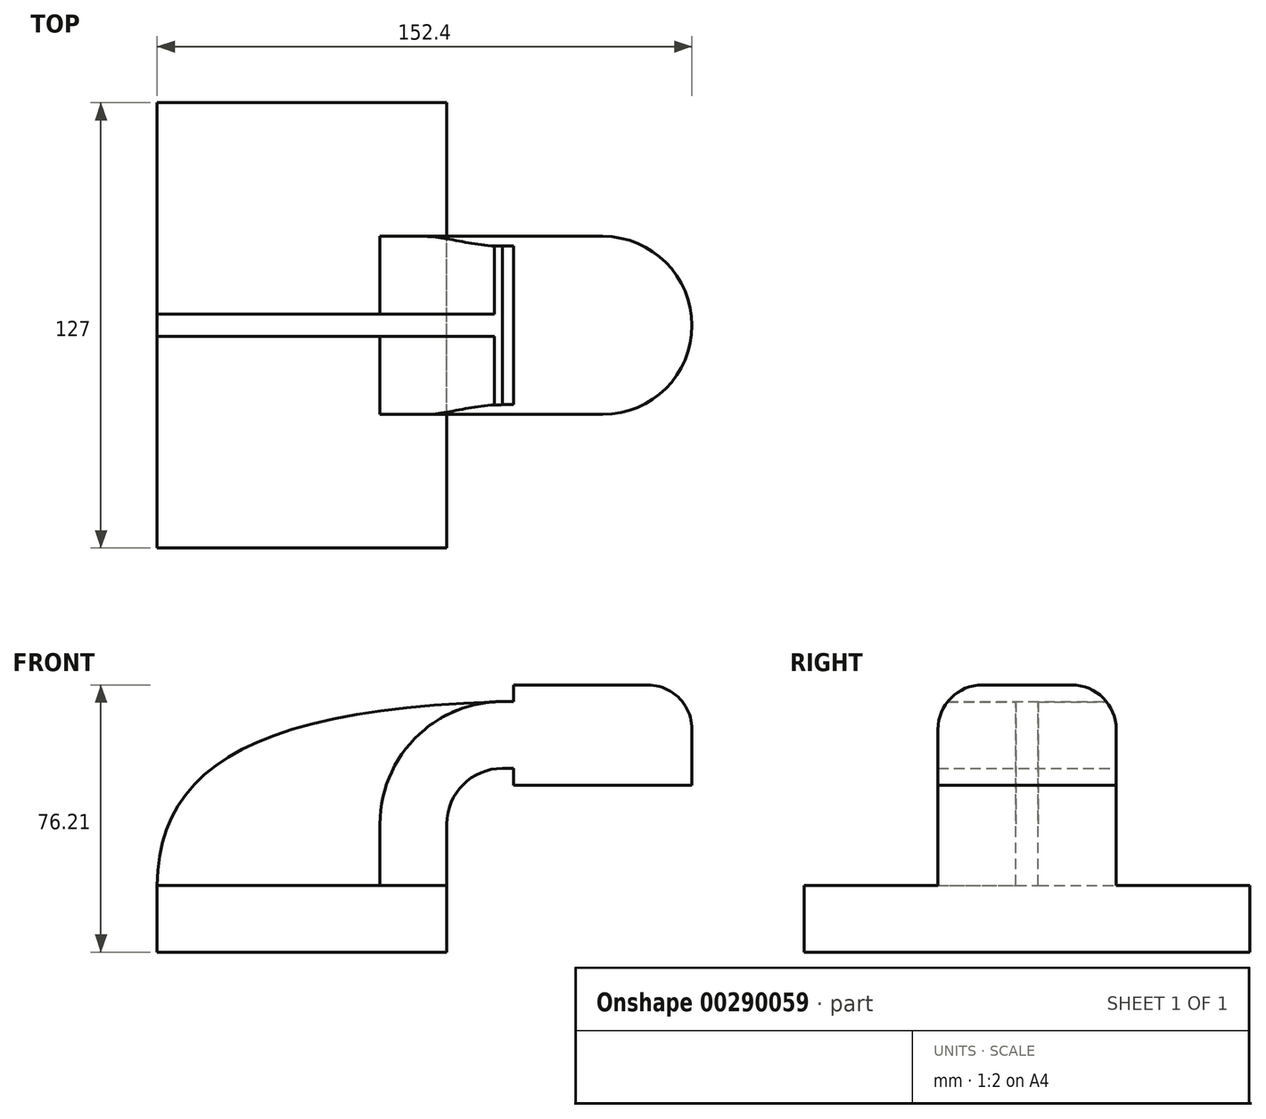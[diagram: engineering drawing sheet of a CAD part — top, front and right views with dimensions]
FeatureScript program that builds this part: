
annotation { "Feature Type Name" : "Feature", "Feature Type Description" : "" }
export const myFeature = defineFeature(function(context is Context, id is Id, definition is map)
    precondition{}
    {
        {
            var Q0;
            Q0=qCreatedBy(makeId("Front.planeOp"),FACE);
            var sketch = newSketch(context, id + "F0", { "sketchPlane" : qUnion([Q0])});
            skLineSegment(sketch, "E0.bottom", {"start": v(-41.28, -9.52) * mm, "end": v(41.28, -9.52) * mm});
            skLineSegment(sketch, "E0.top", {"start": v(-41.28, 9.53) * mm, "end": v(41.28, 9.53) * mm});
            skLineSegment(sketch, "E0.left", {"start": v(-41.28, -9.52) * mm, "end": v(-41.28, 9.53) * mm});
            skLineSegment(sketch, "E0.right", {"start": v(41.28, -9.52) * mm, "end": v(41.28, 9.53) * mm});
            skPoint(sketch, "E0.middle", {"position": v(0, 0) * mm});
            skLineSegment(sketch, "E1.bottom", {"start": v(111.12, 38.1) * mm, "end": v(60.33, 38.1) * mm});
            skLineSegment(sketch, "E1.top", {"start": v(111.13, 66.68) * mm, "end": v(60.33, 66.68) * mm});
            skLineSegment(sketch, "E1.left", {"start": v(111.12, 38.1) * mm, "end": v(111.12, 66.68) * mm});
            skLineSegment(sketch, "E1.right", {"start": v(60.33, 38.1) * mm, "end": v(60.33, 66.68) * mm});
            skPoint(sketch, "E1.middle", {"position": v(85.73, 52.39) * mm});
            skLineSegment(sketch, "E2", {"start": v(41.28, 9.53) * mm, "end": v(41.28, 27) * mm});
            skArc(sketch, "E3", {"start": v(41.28, 27) * mm, "mid": v(45.92, 38.23) * mm, "end": v(57.15, 42.88) * mm});
            skLineSegment(sketch, "E4", {"start": v(57.15, 42.88) * mm, "end": v(85.72, 42.88) * mm});
            skLineSegment(sketch, "E5.0", {"start": v(57.15, 61.93) * mm, "end": v(85.72, 61.93) * mm});
            skArc(sketch, "E5.1", {"start": v(22.23, 27) * mm, "mid": v(32.45, 51.7) * mm, "end": v(57.15, 61.93) * mm});
            skLineSegment(sketch, "E5.2", {"start": v(22.23, 9.53) * mm, "end": v(22.23, 27) * mm});
            skLineSegment(sketch, "E6", {"start": v(85.73, 38.1) * mm, "end": v(85.73, 66.68) * mm});
            skFitSpline(sketch, "E7", {"points": [v(-41.28, 9.53) * mm, v(57.15, 61.93) * mm], "startDerivative": vector(1.5, 100.69) * mm, "endDerivative": vector(213.45, 6.46) * mm});
            skSolve(sketch);
        }
        {
            var Q0;
            Q0=makeQuery(id+"F0.imprint","IMPRINT",FACE,{"disambiguationData":[TD([[makeQuery(id+"F0.imprint","IMPRINT",EDGE,{"derivedFrom":sQuery(id+"F0.wireOp",EDGE,"E0.bottom")}),1.0]])]});
            extrude(context, id + "F1", {"entities" : qUnion([Q0]), "endBound" : BoundingType.SYMMETRIC, "depth" : 127 * mm});
        }
        {
            var Q0;
            {var subQ1=sQuery(id+"F0.wireOp",EDGE,"E2");Q0=makeQuery(id+"F0.imprint","IMPRINT",FACE,{"disambiguationData":[TD([[makeQuery(id+"F0.imprint","IMPRINT",EDGE,{"derivedFrom":subQ1}),1.0]])]});}
            var Q1;
            {var subQ0=sQuery(id+"F0.wireOp",EDGE,"E4");var subQ1=sQuery(id+"F0.wireOp",EDGE,"E1.right");var subQ2=makeQuery(id+"F0.imprint","INTERSECT",VERTEX,{"derivedFrom":[subQ1,subQ0]});Q1=makeQuery(id+"F0.imprint","IMPRINT",FACE,{"disambiguationData":[TD([[makeQuery(id+"F0.imprint","IMPRINT",EDGE,{"disambiguationData":[TD([[subQ2,-1.0]])],"derivedFrom":subQ1}),-1.0]])]});}
            var Q2;
            {var subQ0=sQuery(id+"F0.wireOp",EDGE,"E1.right");var subQ1=sQuery(id+"F0.wireOp",EDGE,"E1.top");var subQ2=makeQuery(id+"F0.imprint","INTERSECT",VERTEX,{"derivedFrom":[subQ1,subQ0]});Q2=makeQuery(id+"F0.imprint","IMPRINT",FACE,{"disambiguationData":[TD([[makeQuery(id+"F0.imprint","IMPRINT",EDGE,{"disambiguationData":[TD([[subQ2,1.0]])],"derivedFrom":subQ1}),1.0]])]});}
            var Q3;
            {var subQ0=sQuery(id+"F0.wireOp",EDGE,"E1.right");var subQ1=sQuery(id+"F0.wireOp",EDGE,"E1.bottom");var subQ2=makeQuery(id+"F0.imprint","INTERSECT",VERTEX,{"derivedFrom":[subQ1,subQ0]});Q3=makeQuery(id+"F0.imprint","IMPRINT",FACE,{"disambiguationData":[TD([[makeQuery(id+"F0.imprint","IMPRINT",EDGE,{"disambiguationData":[TD([[subQ2,1.0]])],"derivedFrom":subQ1}),-1.0]])]});}
            extrude(context, id + "F2", {"entities" : qUnion([Q0, Q1, Q2, Q3]), "operationType" : NewBodyOperationType.ADD, "endBound" : BoundingType.SYMMETRIC, "depth" : 50.8 * mm});
        }
        {
            var Q0;
            {var subQ0=sQuery(id+"F0.wireOp",EDGE,"E1.left");Q0=makeQuery(id+"F0.imprint","IMPRINT",FACE,{"disambiguationData":[TD([[makeQuery(id+"F0.imprint","IMPRINT",EDGE,{"derivedFrom":subQ0}),1.0]])]});}
            var Q1;
            Q1=sQuery(id+"F0.wireOp",EDGE,"E6");
            revolve(context, id + "F3", {"operationType" : NewBodyOperationType.ADD, "entities" : qUnion([Q0]), "axis" : qUnion([Q1]), "revolveType" : RevolveType.FULL});
        }
        {
            var Q0;
            {var subQ3=sQuery(id+"F0.wireOp",EDGE,"E5.2");Q0=makeQuery(id+"F0.imprint","IMPRINT",FACE,{"disambiguationData":[TD([[makeQuery(id+"F0.imprint","IMPRINT",EDGE,{"derivedFrom":subQ3}),1.0]])]});}
            extrude(context, id + "F4", {"entities" : qUnion([Q0]), "operationType" : NewBodyOperationType.ADD, "endBound" : BoundingType.SYMMETRIC, "depth" : 6.35 * mm});
        }
        {
            var Q0;
            Q0=makeQuery(id+"F3.opRevolve","SWEPT_EDGE",EDGE,{"disambiguationData":[OSD([sQuery(id+"F0.wireOp",EDGE,"E1.top"),sQuery(id+"F0.wireOp",EDGE,"E1.left")])]});
            fillet(context, id + "F5", {"entities" : qUnion([Q0]), "radius" : 12.7 * mm, "tangentPropagation" : true, "allowEdgeOverflow" : false});
        }
    });
